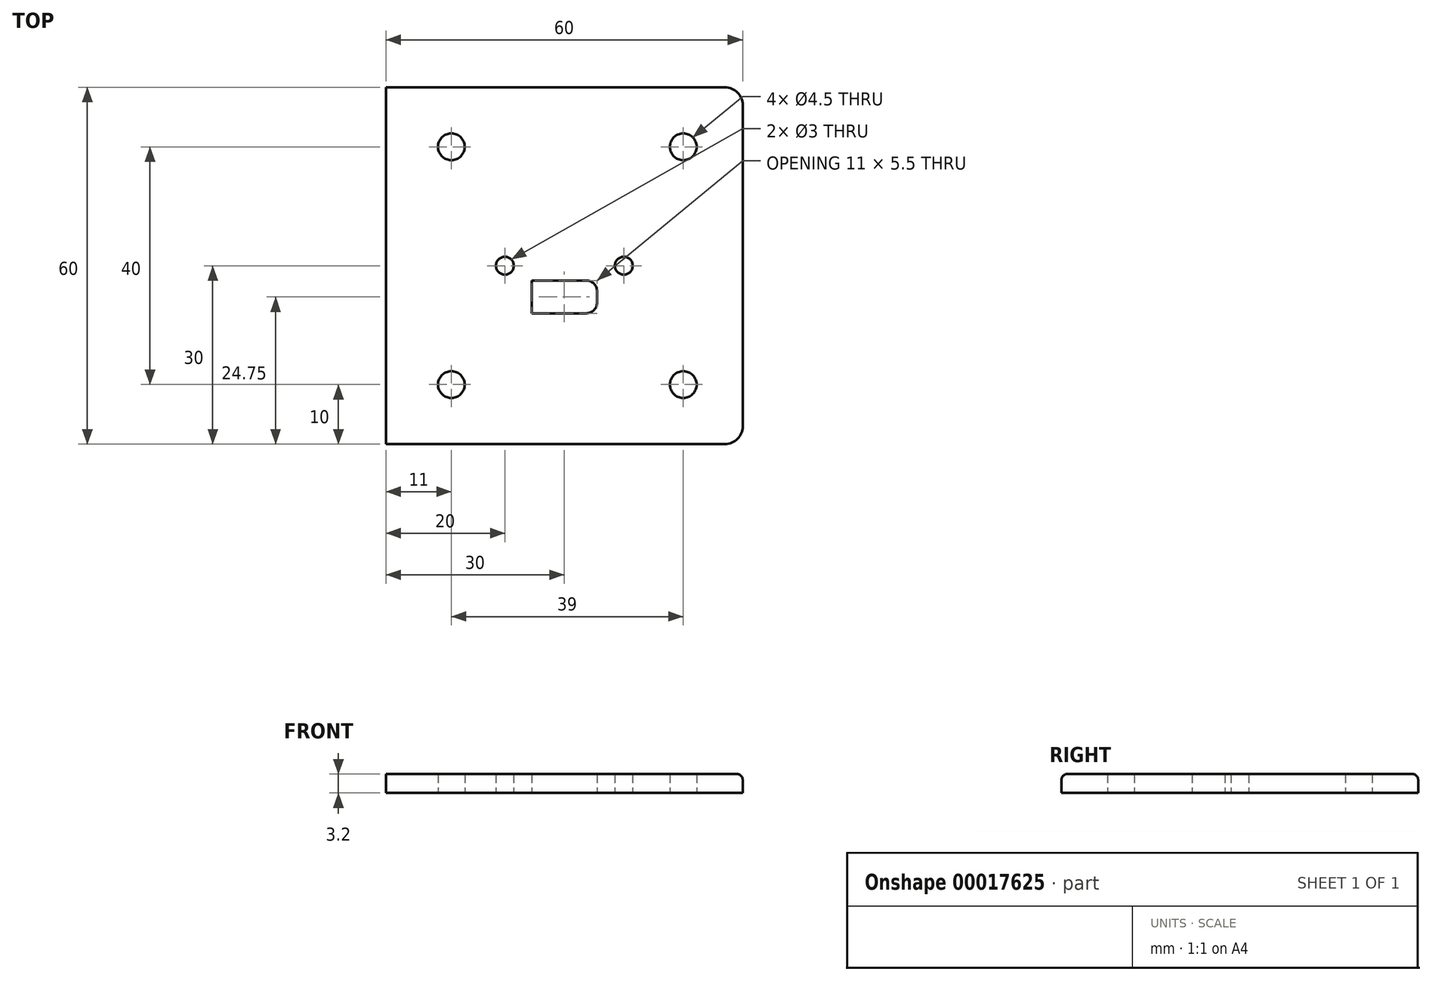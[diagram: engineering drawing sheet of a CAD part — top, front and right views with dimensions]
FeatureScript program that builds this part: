
annotation { "Feature Type Name" : "Feature", "Feature Type Description" : "" }
export const myFeature = defineFeature(function(context is Context, id is Id, definition is map)
    precondition{}
    {
        {
            var Q0;
            Q0=qCreatedBy(makeId("Top.planeOp"),FACE);
            var sketch = newSketch(context, id + "F0", { "sketchPlane" : qUnion([Q0])});
            skLineSegment(sketch, "E0.rect.right", {"start": v(30, -30) * mm, "end": v(30, 30) * mm});
            skPoint(sketch, "E0.rect.middle", {"position": v(0, 0) * mm});
            skCircle(sketch, "E1", {"center": v(-19, -20) * mm, "radius": 2.25 * mm});
            skCircle(sketch, "E2", {"center": v(-19, 20) * mm, "radius": 2.25 * mm});
            skCircle(sketch, "E3", {"center": v(20, 20) * mm, "radius": 2.25 * mm});
            skCircle(sketch, "E4", {"center": v(20, -20) * mm, "radius": 2.25 * mm});
            skLineSegment(sketch, "E5", {"start": v(-30, 30) * mm, "end": v(-30, -30) * mm});
            skLineSegment(sketch, "E6", {"start": v(-30, 30) * mm, "end": v(30, 30) * mm});
            skLineSegment(sketch, "E7", {"start": v(-30, -30) * mm, "end": v(30, -30) * mm});
            skLineSegment(sketch, "E8.bottom", {"start": v(-30, -30) * mm, "end": v(-5.5, -30) * mm});
            skLineSegment(sketch, "E8.top", {"start": v(-30, 30) * mm, "end": v(-5.5, 30) * mm});
            skLineSegment(sketch, "E8.left", {"start": v(-30, -30) * mm, "end": v(-30, 30) * mm});
            skLineSegment(sketch, "E8.right", {"start": v(-5.5, -8) * mm, "end": v(-5.5, -2.5) * mm});
            skLineSegment(sketch, "E9.bottom", {"start": v(30, -30) * mm, "end": v(5.5, -30) * mm});
            skLineSegment(sketch, "E9.top", {"start": v(30, 30) * mm, "end": v(5.5, 30) * mm});
            skLineSegment(sketch, "E9.right", {"start": v(5.5, -8) * mm, "end": v(5.5, -2.5) * mm});
            skLineSegment(sketch, "E10.bottom", {"start": v(-5.5, -30) * mm, "end": v(3.5, -30) * mm});
            skLineSegment(sketch, "E10.top", {"start": v(-5.5, -8) * mm, "end": v(5.5, -8) * mm});
            skLineSegment(sketch, "E11.top", {"start": v(-5.5, -2.5) * mm, "end": v(5.5, -2.5) * mm});
            skCircle(sketch, "E12", {"center": v(-10, 0) * mm, "radius": 1.5 * mm});
            skCircle(sketch, "E13", {"center": v(10, 0) * mm, "radius": 1.5 * mm});
            skSolve(sketch);
        }
        {
            var Q0;
            Q0=makeQuery(id+"F0.imprint","IMPRINT",FACE,{"disambiguationData":[TD([[makeQuery(id+"F0.imprint","IMPRINT",EDGE,{"derivedFrom":sQuery(id+"F0.wireOp",EDGE,"E1")}),-1.0]])]});
            extrude(context, id + "F1", {"entities" : qUnion([Q0]), "depth" : 3.2 * mm, "offsetDistance" : 25 * mm});
        }
        {
            var Q0;
            Q0=makeQuery(id+"F1.opExtrude","SWEPT_EDGE",EDGE,{"disambiguationData":[OSD([sQuery(id+"F0.wireOp",EDGE,"E8.top"),sQuery(id+"F0.wireOp",EDGE,"E8.left")])]});
            var Q1;
            Q1=makeQuery(id+"F1.opExtrude","SWEPT_EDGE",EDGE,{"disambiguationData":[OSD([sQuery(id+"F0.wireOp",EDGE,"E8.bottom"),sQuery(id+"F0.wireOp",EDGE,"E8.left")])]});
            var Q2;
            Q2=makeQuery(id+"F1.opExtrude","SWEPT_EDGE",EDGE,{"disambiguationData":[OSD([sQuery(id+"F0.wireOp",EDGE,"E9.bottom"),sQuery(id+"F0.wireOp",EDGE,"E0.rect.right")])]});
            var Q3;
            Q3=makeQuery(id+"F1.opExtrude","SWEPT_EDGE",EDGE,{"disambiguationData":[OSD([sQuery(id+"F0.wireOp",EDGE,"E9.top"),sQuery(id+"F0.wireOp",EDGE,"E0.rect.right")])]});
            fillet(context, id + "F2", {"entities" : qUnion([Q0, Q1, Q2, Q3]), "radius" : 3 * mm, "tangentPropagation" : true, "allowEdgeOverflow" : false});
        }
        {
            var Q0;
            Q0=makeQuery(id+"F1.opExtrude","SWEPT_EDGE",EDGE,{"disambiguationData":[OSD([sQuery(id+"F0.wireOp",EDGE,"E11.top"),sQuery(id+"F0.wireOp",EDGE,"E9.right")])]});
            var Q1;
            Q1=makeQuery(id+"F1.opExtrude","SWEPT_EDGE",EDGE,{"disambiguationData":[OSD([sQuery(id+"F0.wireOp",EDGE,"E10.top"),sQuery(id+"F0.wireOp",EDGE,"E9.right")])]});
            fillet(context, id + "F3", {"entities" : qUnion([Q0, Q1]), "radius" : 1.8 * mm, "tangentPropagation" : true, "allowEdgeOverflow" : false});
        }
        {
            var Q0;
            Q0=makeQuery(id+"F1.opExtrude","CAP_EDGE",EDGE,{"disambiguationData":[OSD([sQuery(id+"F0.wireOp",EDGE,"E6"),sQuery(id+"F0.wireOp",EDGE,"E8.top"),sQuery(id+"F0.wireOp",EDGE,"E9.top")])],"isStart":false});
            var Q1;
            {var subQ0=sQuery(id+"F0.wireOp",EDGE,"E8.left");var subQ1=sQuery(id+"F0.wireOp",EDGE,"E8.top");Q1=makeQuery(id+"F2.opFillet","BLEND_EDGE",EDGE,{"blendedFrom":[makeQuery(id+"F1.opExtrude","SWEPT_EDGE",EDGE,{"disambiguationData":[OSD([subQ1,subQ0])]}),makeQuery(id+"F1.opExtrude","CAP_FACE",FACE,{"disambiguationData":[OSD([sQuery(id+"F0.wireOp",EDGE,"E1"),sQuery(id+"F0.wireOp",EDGE,"E2"),sQuery(id+"F0.wireOp",EDGE,"E3"),sQuery(id+"F0.wireOp",EDGE,"E4"),sQuery(id+"F0.wireOp",EDGE,"E6"),sQuery(id+"F0.wireOp",EDGE,"E7"),sQuery(id+"F0.wireOp",EDGE,"E8.bottom"),subQ1,subQ0,sQuery(id+"F0.wireOp",EDGE,"E9.bottom"),sQuery(id+"F0.wireOp",EDGE,"E9.top"),sQuery(id+"F0.wireOp",EDGE,"E0.rect.right"),sQuery(id+"F0.wireOp",EDGE,"E10.bottom"),sQuery(id+"F0.wireOp",EDGE,"E10.top"),sQuery(id+"F0.wireOp",EDGE,"E11.top"),sQuery(id+"F0.wireOp",EDGE,"E8.right"),sQuery(id+"F0.wireOp",EDGE,"E9.right"),sQuery(id+"F0.wireOp",EDGE,"E12"),sQuery(id+"F0.wireOp",EDGE,"E13")])],"isStart":false})],"blendedInto":[makeQuery(id+"F1.opExtrude","CAP_FACE",FACE,{"disambiguationData":[OSD([sQuery(id+"F0.wireOp",EDGE,"E1"),sQuery(id+"F0.wireOp",EDGE,"E2"),sQuery(id+"F0.wireOp",EDGE,"E3"),sQuery(id+"F0.wireOp",EDGE,"E4"),sQuery(id+"F0.wireOp",EDGE,"E6"),sQuery(id+"F0.wireOp",EDGE,"E7"),sQuery(id+"F0.wireOp",EDGE,"E8.bottom"),subQ1,subQ0,sQuery(id+"F0.wireOp",EDGE,"E9.bottom"),sQuery(id+"F0.wireOp",EDGE,"E9.top"),sQuery(id+"F0.wireOp",EDGE,"E0.rect.right"),sQuery(id+"F0.wireOp",EDGE,"E10.bottom"),sQuery(id+"F0.wireOp",EDGE,"E10.top"),sQuery(id+"F0.wireOp",EDGE,"E11.top"),sQuery(id+"F0.wireOp",EDGE,"E8.right"),sQuery(id+"F0.wireOp",EDGE,"E9.right"),sQuery(id+"F0.wireOp",EDGE,"E12"),sQuery(id+"F0.wireOp",EDGE,"E13")])],"isStart":false})]});}
            fillet(context, id + "F4", {"entities" : qUnion([Q0, Q1]), "radius" : 1 * mm, "tangentPropagation" : true, "allowEdgeOverflow" : false});
        }
    });
